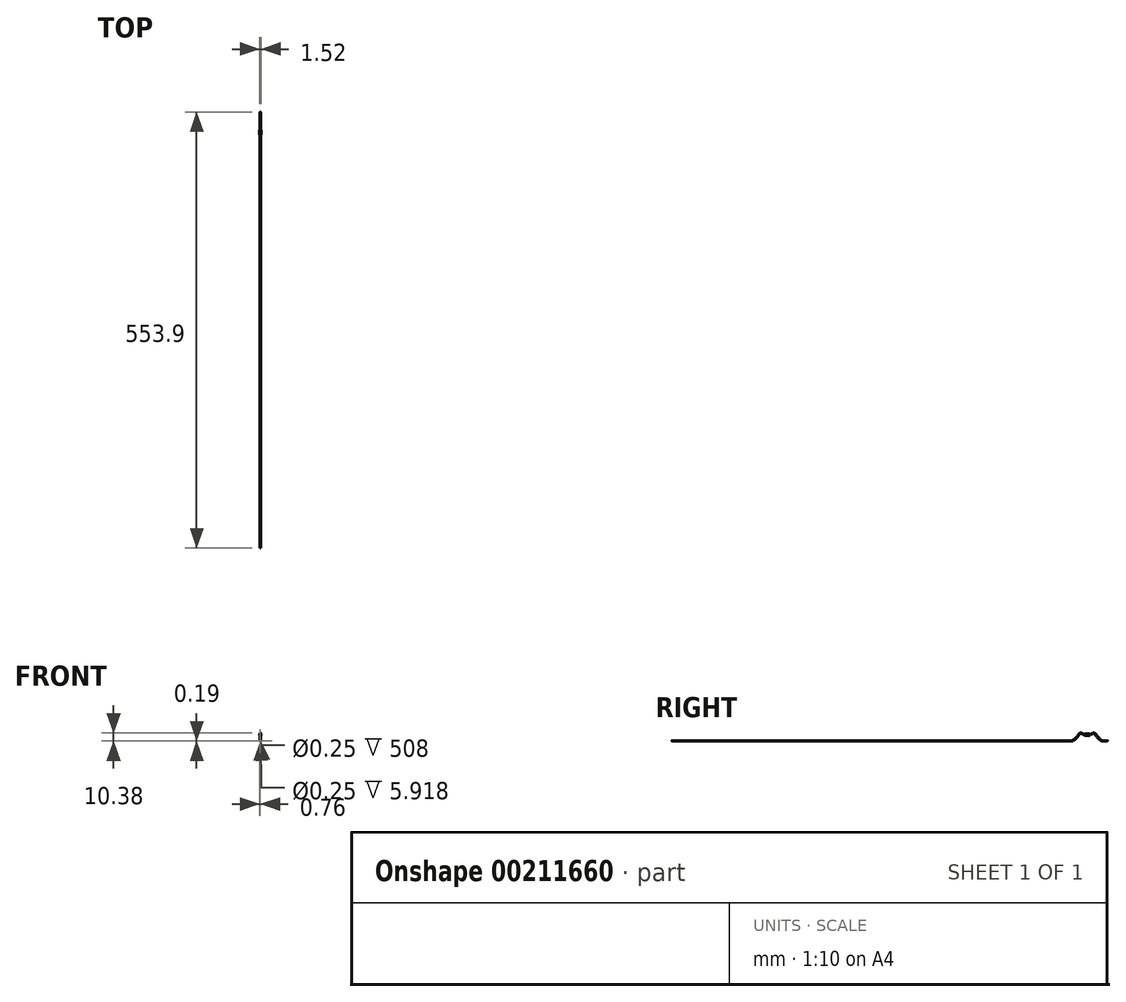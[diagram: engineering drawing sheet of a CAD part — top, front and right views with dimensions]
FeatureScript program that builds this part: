
annotation { "Feature Type Name" : "Feature", "Feature Type Description" : "" }
export const myFeature = defineFeature(function(context is Context, id is Id, definition is map)
    precondition{}
    {
        {
            var Q0;
            Q0=qCreatedBy(makeId("Right.planeOp"),FACE);
            var sketch = newSketch(context, id + "F0", { "sketchPlane" : qUnion([Q0])});
            skLineSegment(sketch, "E0", {"start": v(0, 0) * mm, "end": v(-5.92, 0) * mm});
            skFitSpline(sketch, "E1", {"points": [v(-5.92, 0) * mm, v(-12.52, 4.7) * mm, v(-17.72, 10) * mm, v(-22.86, 7.87) * mm], "startDerivative": vector(-13.48, 0) * mm, "endDerivative": vector(-16.5, 0) * mm});
            skLineSegment(sketch, "E2", {"start": v(-22.86, 7.87) * mm, "end": v(-28.96, 7.87) * mm});
            skLineSegment(sketch, "E3", {"start": v(-25.9, 37.72) * mm, "end": v(-25.9, -23.67) * mm, "construction": true});
            skPoint(sketch, "E4", {"position": v(-25.9, 7.87) * mm});
            skFitSpline(sketch, "E5.MirrorCS", {"points": [v(-45.9, 0) * mm, v(-39.3, 4.7) * mm, v(-34.1, 10) * mm, v(-28.96, 7.87) * mm], "startDerivative": vector(13.48, 0) * mm, "endDerivative": vector(16.5, 0) * mm});
            skLineSegment(sketch, "E6", {"start": v(-45.9, 0) * mm, "end": v(-553.9, 0) * mm});
            skLineSegment(sketch, "E7", {"start": v(-40.86, 10) * mm, "end": v(-7.56, 10) * mm, "construction": true});
            skSolve(sketch);
        }
        {
            var Q0;
            Q0=qCreatedBy(makeId("Front.planeOp"),FACE);
            var sketch = newSketch(context, id + "F1", { "sketchPlane" : qUnion([Q0])});
            skCircle(sketch, "E8", {"center": v(0, -0.2) * mm, "radius": 0.2 * mm});
            skCircle(sketch, "E9", {"center": v(0, -0.2) * mm, "radius": 0.13 * mm});
            skSolve(sketch);
        }
        {
            var Q0;
            Q0=qSketchRegion(id+"F1",true);
            var Q1;
            Q1=qConstructionFilter(qBodyType(qCreatedBy(id+"F0",EDGE),BodyType.WIRE),ConstructionObject.NO);
            sweep(context, id + "F2", {"profiles" : qUnion([Q0]), "path" : qUnion([Q1])});
        }
        {
            var Q0;
            Q0=qCreatedBy(makeId("Front.planeOp"),FACE);
            cPlane(context, id + "F3", {"entities" : qUnion([Q0]), "cplaneType" : CPlaneType.OFFSET, "offset" : 22.86 * mm, "width" : 152.4 * mm, "height" : 152.4 * mm});
        }
        {
            var Q0;
            Q0=qCreatedBy(id+"F3.planeOp",FACE);
            var sketch = newSketch(context, id + "F4", { "sketchPlane" : qUnion([Q0])});
            skCircle(sketch, "E10.0", {"center": v(0, 7.68) * mm, "radius": 0.2 * mm, "construction": true});
            skCircle(sketch, "E11", {"center": v(0, 7.68) * mm, "radius": 0.76 * mm});
            skSolve(sketch);
        }
        {
            var Q0;
            Q0=qSketchRegion(id+"F4",true);
            extrude(context, id + "F5", {"entities" : qUnion([Q0]), "operationType" : NewBodyOperationType.ADD, "depth" : 6.1 * mm});
        }
    });
